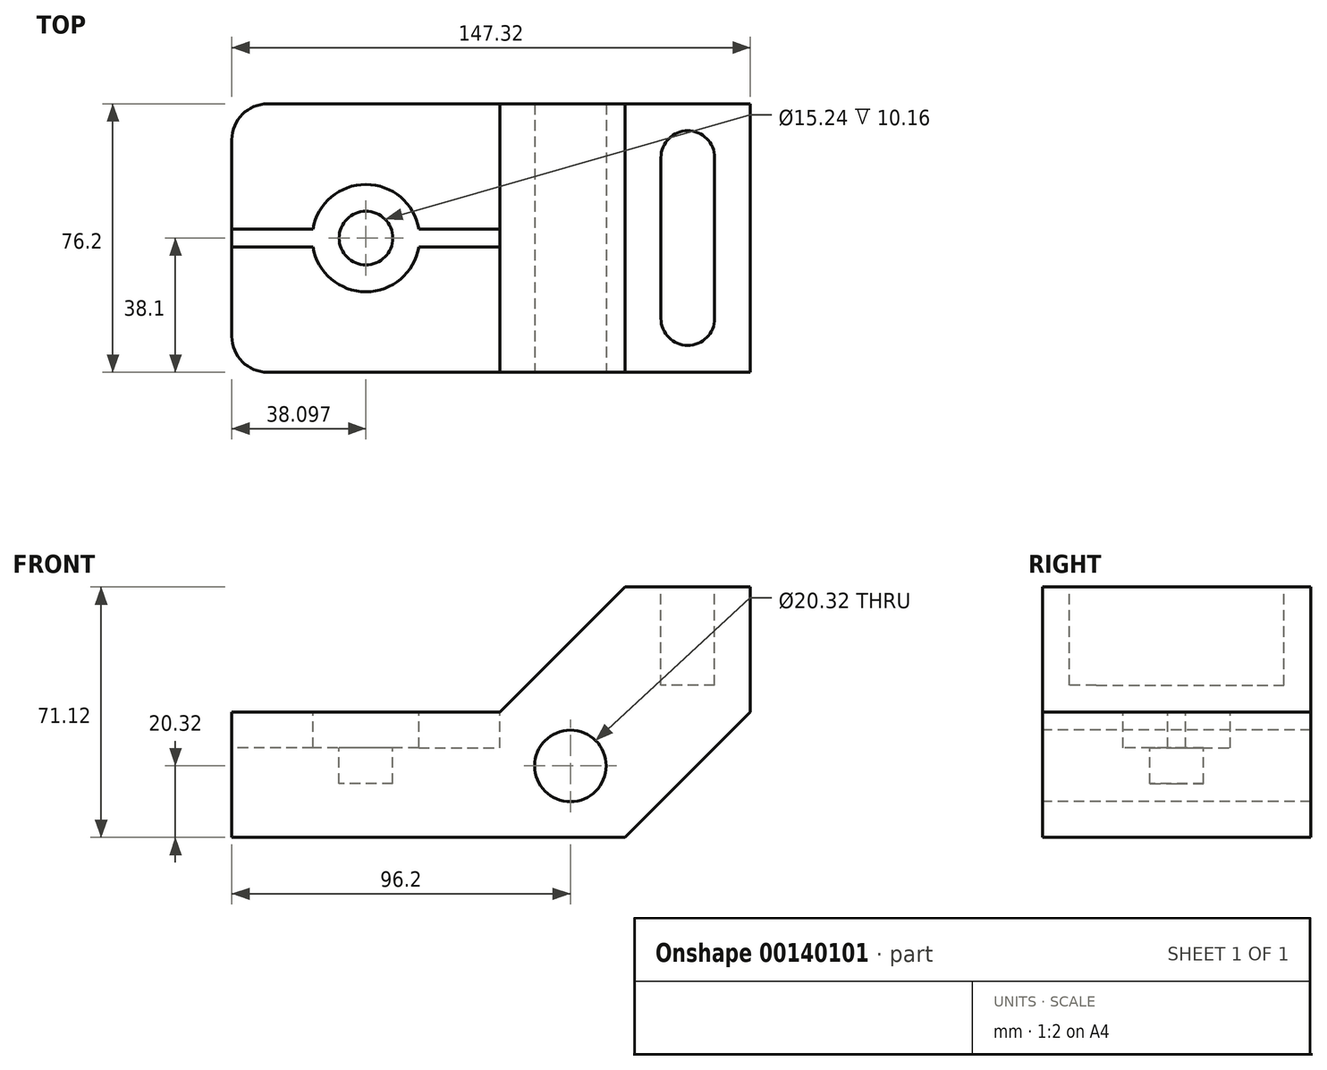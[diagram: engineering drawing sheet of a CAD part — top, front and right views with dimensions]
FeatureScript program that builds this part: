
annotation { "Feature Type Name" : "Feature", "Feature Type Description" : "" }
export const myFeature = defineFeature(function(context is Context, id is Id, definition is map)
    precondition{}
    {
        {
            var Q0;
            Q0=qCreatedBy(makeId("Front.planeOp"),FACE);
            var sketch = newSketch(context, id + "F0", { "sketchPlane" : qUnion([Q0])});
            skLineSegment(sketch, "E0", {"start": v(-96.2, -20.32) * mm, "end": v(15.56, -20.32) * mm});
            skLineSegment(sketch, "E1", {"start": v(15.56, -20.32) * mm, "end": v(51.12, 15.24) * mm});
            skLineSegment(sketch, "E2", {"start": v(51.12, 15.24) * mm, "end": v(51.12, 50.8) * mm});
            skLineSegment(sketch, "E3", {"start": v(51.12, 50.8) * mm, "end": v(15.56, 50.8) * mm});
            skLineSegment(sketch, "E4", {"start": v(15.56, 50.8) * mm, "end": v(-20, 15.24) * mm});
            skLineSegment(sketch, "E5", {"start": v(-20, 15.24) * mm, "end": v(-96.2, 15.24) * mm});
            skLineSegment(sketch, "E6", {"start": v(-96.2, 15.24) * mm, "end": v(-96.2, -20.32) * mm});
            skCircle(sketch, "E7", {"center": v(0, 0) * mm, "radius": 10.16 * mm});
            skSolve(sketch);
        }
        {
            var Q0;
            Q0 = qSketchRegion(id + "F0", true);
            extrude(context, id + "F1", {"entities" : qUnion([Q0]), "oppositeDirection" : true, "depth" : 76.2 * mm});
        }
        {
            var Q0;
            Q0=makeQuery(id+"F1.opExtrude","SWEPT_FACE",FACE,{"disambiguationData":[OSD([sQuery(id+"F0.wireOp",EDGE,"E3")])]});
            var sketch = newSketch(context, id + "F2", { "sketchPlane" : qUnion([Q0])});
            skLineSegment(sketch, "E8.left", {"start": v(40.96, 15.24) * mm, "end": v(40.96, 60.96) * mm});
            skLineSegment(sketch, "E8.right", {"start": v(25.72, 15.24) * mm, "end": v(25.72, 60.96) * mm});
            skArc(sketch, "E9", {"start": v(40.96, 60.96) * mm, "mid": v(33.34, 68.58) * mm, "end": v(25.72, 60.96) * mm});
            skArc(sketch, "E10", {"start": v(25.72, 15.24) * mm, "mid": v(33.34, 7.62) * mm, "end": v(40.96, 15.24) * mm});
            skSolve(sketch);
        }
        {
            var Q0;
            Q0 = qSketchRegion(id + "F2", true);
            extrude(context, id + "F3", {"entities" : qUnion([Q0]), "operationType" : NewBodyOperationType.REMOVE, "oppositeDirection" : true, "depth" : 27.94 * mm});
        }
        {
            var Q0;
            Q0=makeQuery(id+"F1.opExtrude","SWEPT_FACE",FACE,{"disambiguationData":[OSD([sQuery(id+"F0.wireOp",EDGE,"E5")])]});
            var sketch = newSketch(context, id + "F4", { "sketchPlane" : qUnion([Q0])});
            skArc(sketch, "E11", {"start": v(-43.08, 40.64) * mm, "mid": v(-58.1, 53.34) * mm, "end": v(-73.13, 40.64) * mm});
            skLineSegment(sketch, "E12", {"start": v(-43.08, 40.64) * mm, "end": v(-20, 40.64) * mm});
            skLineSegment(sketch, "E13", {"start": v(-43.08, 35.56) * mm, "end": v(-20, 35.56) * mm});
            skLineSegment(sketch, "E14", {"start": v(-73.13, 40.64) * mm, "end": v(-96.2, 40.64) * mm});
            skLineSegment(sketch, "E15", {"start": v(-73.13, 35.56) * mm, "end": v(-96.2, 35.56) * mm});
            skArc(sketch, "E16.trimOffspring", {"start": v(-73.13, 35.56) * mm, "mid": v(-58.1, 22.86) * mm, "end": v(-43.08, 35.56) * mm});
            skPoint(sketch, "E17", {"position": v(-96.2, 38.1) * mm});
            skLineSegment(sketch, "E18", {"start": v(-96.2, 38.1) * mm, "end": v(-20, 38.1) * mm, "construction": true});
            skLineSegment(sketch, "E19", {"start": v(-96.2, 35.56) * mm, "end": v(-96.2, 40.64) * mm});
            skLineSegment(sketch, "E20", {"start": v(-20, 35.56) * mm, "end": v(-20, 40.64) * mm});
            skSolve(sketch);
        }
        {
            var Q0;
            Q0 = qSketchRegion(id + "F4", true);
            extrude(context, id + "F5", {"entities" : qUnion([Q0]), "operationType" : NewBodyOperationType.REMOVE, "oppositeDirection" : true, "depth" : 10.16 * mm});
        }
        {
            var Q0;
            Q0=makeQuery(id+"F5.boolean.opBoolean","COPY",FACE,{"derivedFrom":makeQuery(id+"F5.opExtrude","CAP_FACE",FACE,{"disambiguationData":[OSD([sQuery(id+"F4.wireOp",EDGE,"E11"),sQuery(id+"F4.wireOp",EDGE,"E12"),sQuery(id+"F4.wireOp",EDGE,"E13"),sQuery(id+"F4.wireOp",EDGE,"E14"),sQuery(id+"F4.wireOp",EDGE,"E15"),sQuery(id+"F4.wireOp",EDGE,"E16.trimOffspring"),sQuery(id+"F4.wireOp",EDGE,"E19"),sQuery(id+"F4.wireOp",EDGE,"E20")])],"isStart":false})});
            var sketch = newSketch(context, id + "F6", { "sketchPlane" : qUnion([Q0])});
            skCircle(sketch, "E21", {"center": v(-58.1, 38.1) * mm, "radius": 7.62 * mm});
            skSolve(sketch);
        }
        {
            var Q0;
            Q0 = qSketchRegion(id + "F6", true);
            var Q1;
            Q1=makeQuery(id+"F1.opExtrude","SWEPT_FACE",FACE,{"disambiguationData":[OSD([sQuery(id+"F0.wireOp",EDGE,"E0")])]});
            extrude(context, id + "F7", {"entities" : qUnion([Q0]), "operationType" : NewBodyOperationType.REMOVE, "oppositeDirection" : true, "endBoundEntityFace" : qUnion([Q1]), "depth" : 10.16 * mm});
        }
        {
            var Q0;
            Q0=makeQuery(id+"F1.opExtrude","CAP_EDGE",EDGE,{"disambiguationData":[OSD([sQuery(id+"F0.wireOp",EDGE,"E6")])],"isStart":true});
            var Q1;
            Q1=makeQuery(id+"F1.opExtrude","CAP_EDGE",EDGE,{"disambiguationData":[OSD([sQuery(id+"F0.wireOp",EDGE,"E6")])],"isStart":false});
            fillet(context, id + "F8", {"entities" : qUnion([Q0, Q1]), "radius" : 10.16 * mm, "tangentPropagation" : true, "allowEdgeOverflow" : false});
        }
    });
